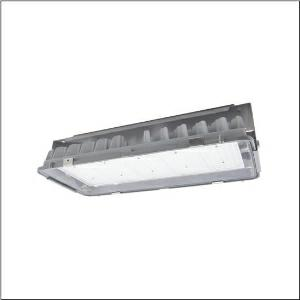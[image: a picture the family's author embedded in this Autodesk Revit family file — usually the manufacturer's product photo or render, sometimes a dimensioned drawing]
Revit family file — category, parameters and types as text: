
# Revit family: highbay_11xtreme_51hf62da4mma
name_source: partatom
category: Lighting Fixtures
units: mm (PartAtom-declared; Revit-internal decimal feet)

## family parameters
Cut with Voids When Loaded = No
Host = Face
Light Source = No
Part Type = Normal
Room Calculation Point = No
Round Connector Dimension = Use Diameter
Shared = No

## types (1)
- --- (1 x LED, 31100 lm, 170.9 W, 4000K)
    Apparent Load = 171 VA
    CIE Flux Codes = 84 96 100 100 100
    Color Rendering = 80
    Color Temperature = 4000K
    Default Elevation = 1800 mm
    Description = Highbay 11Xtreme, high bay luminaire, primary light control with lens, of PMMA, primary optical cover: cover, of toughened safety glass, light emission: direct distribution, primary light characteristic: symmetric, installation type: suspended mounting, surface-mounted, 1x LED module,for 1x LED, rated luminous flux: 31.100lm, luminous efficacy: 182lm/W, light colour: 840, colour temperature: 4000K, control gear: DALI 2, with cable H07RN-F 5x 1.5mm², mains connection: 220..240V, AC, 50/60Hz, cable length: 1,5m, rated input power: 171W, luminaire housing, of diecast aluminium, coated, silver, length: 595mm, width: 280mm, height: 195mm, protection rating (complete): IP66, insulation class (complete): insulation class I (protective earthing), certification: CE, ENEC, UKCA, protection symbol: D, ball protection: ball impact resistant according to DIN VDE 0710 part 13 (with chain suspension), impact resistance: IK08, permissible operating ambient temperature: -25..+60°C, reducing of maximum allowable ambient temperature of 5°C with ceiling mounting, packaging unit: 1 piece
    Height = 157 mm
    Lamp = 1 x LED
    Lamp Light Flux = 31100 lm
    Lamp Power = 170.9 W
    Lamp count = 1
    Length = 593 mm
    Luminous efficacy = 182 lm/W
    Manufacturer = Siteco
    ModVariant = No
    Model = 51HF62DA4MMA
    Mounting Place = Ceiling
    Mounting Type = Pendant
    Number of Poles = 1
    OnlyDefault = Yes
    Power Factor = 1
    Product Name = Highbay 11Xtreme
    Product group = high bay luminaire
    ProductGroupID = 902
    Protection Class = Protection class I
    Protection Degree = IP 66
    RLX_Detail_Level = 1
    RLX_Emergency_Light_Flux = 0 lm
    RLX_Emergency_Type = 0
    RLX_Emergency_Type_DB = No
    RlxData = <blob elided: 28369 chars, md5=5f78ebdd>
    Socket = socket
    Standby Power = 0 W
    System Light Flux = 31100 lm
    System Power = 171 W
    Type Comments = factory setting: luminous flux: 100 % | dim-lin: 254 | 1133 mA
    Type Image = l_1258342.jpg
    URL = http://relux.com
    VarID = @adj_088281
    Voltage = 0 V
    Weight = 0.00 kg
    Width = 568 mm

## geometry (parser evidence)
native form markers: Blend x4, Sweep x9
no freeform markers — native parametric forms only
